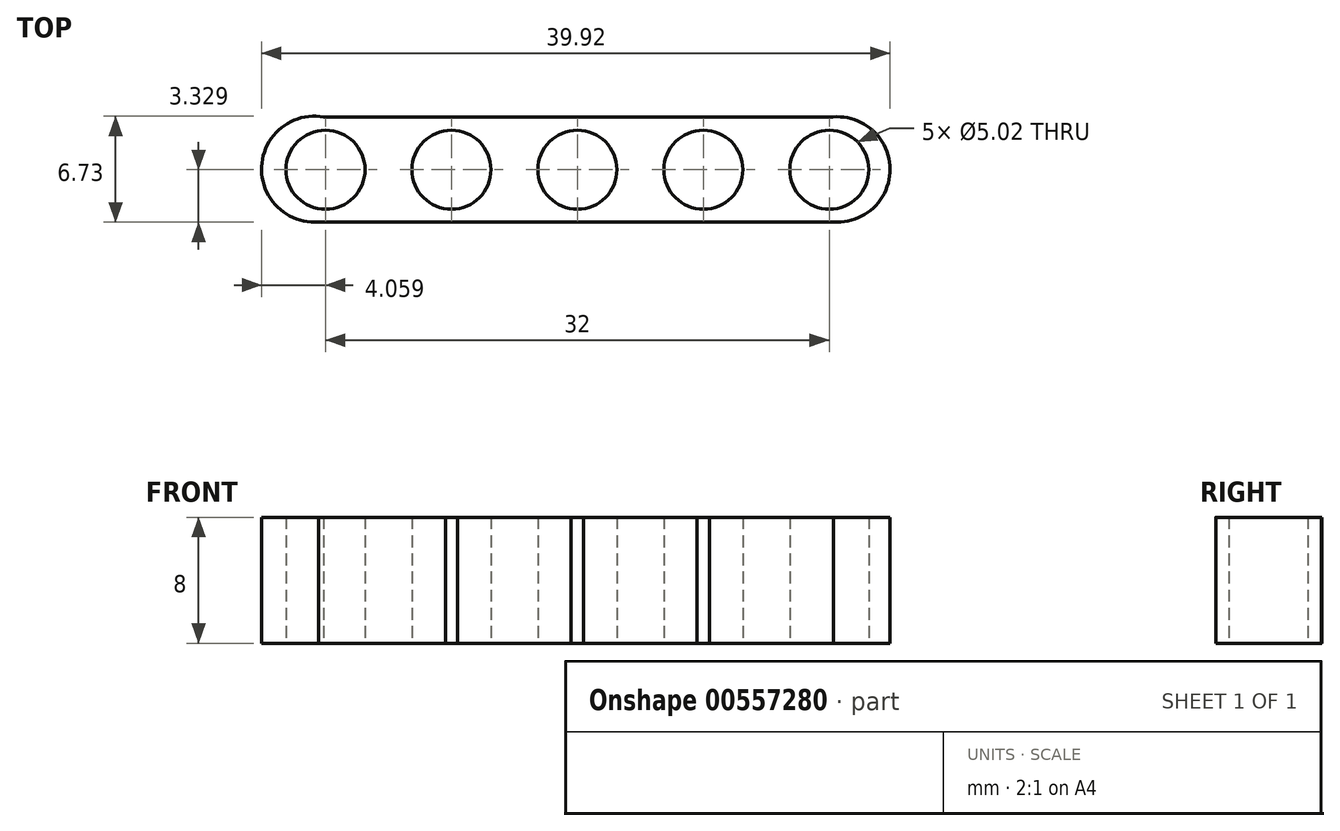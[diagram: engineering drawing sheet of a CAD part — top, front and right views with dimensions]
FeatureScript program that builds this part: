
annotation { "Feature Type Name" : "Feature", "Feature Type Description" : "" }
export const myFeature = defineFeature(function(context is Context, id is Id, definition is map)
    precondition{}
    {
        {
            var Q0;
            Q0=qCreatedBy(makeId("Top.planeOp"),FACE);
            var sketch = newSketch(context, id + "F0", { "sketchPlane" : qUnion([Q0])});
            skArc(sketch, "E0", {"start": v(14.35, -2.5) * mm, "mid": v(17.95, 0.86) * mm, "end": v(14.32, 4.17) * mm});
            skArc(sketch, "E1", {"start": v(-18.03, 4.17) * mm, "mid": v(-21.97, 1.02) * mm, "end": v(-18.35, -2.5) * mm});
            skLineSegment(sketch, "E2", {"start": v(-18.03, 4.17) * mm, "end": v(14.32, 4.17) * mm});
            skLineSegment(sketch, "E3", {"start": v(-18.35, -2.5) * mm, "end": v(14.35, -2.5) * mm});
            skCircle(sketch, "E4.2.0.1", {"center": v(14.09, 0.82) * mm, "radius": 2.5 * mm});
            skCircle(sketch, "E5.1.0.0", {"center": v(6.09, 0.82) * mm, "radius": 2.5 * mm});
            skCircle(sketch, "E5.1.0.1", {"center": v(6.09, 0.82) * mm, "radius": 3.33 * mm});
            skCircle(sketch, "E5.2.0.0", {"center": v(-1.91, 0.82) * mm, "radius": 2.5 * mm});
            skCircle(sketch, "E5.2.0.1", {"center": v(-1.91, 0.82) * mm, "radius": 3.33 * mm});
            skCircle(sketch, "E5.3.0.0", {"center": v(-9.91, 0.82) * mm, "radius": 2.5 * mm});
            skCircle(sketch, "E5.3.0.1", {"center": v(-9.91, 0.82) * mm, "radius": 3.33 * mm});
            skCircle(sketch, "E5.4.0.0", {"center": v(-17.91, 0.82) * mm, "radius": 2.5 * mm});
            skLineSegment(sketch, "E5.direction1", {"start": v(14.09, 0.82) * mm, "end": v(6.09, 0.82) * mm, "construction": true});
            skSolve(sketch);
        }
        {
            var Q0;
            Q0 = qSketchRegion(id + "F0", true);
            extrude(context, id + "F1", {"entities" : qUnion([Q0]), "depth" : 8 * mm, "offsetDistance" : 25.4 * mm});
        }
    });
